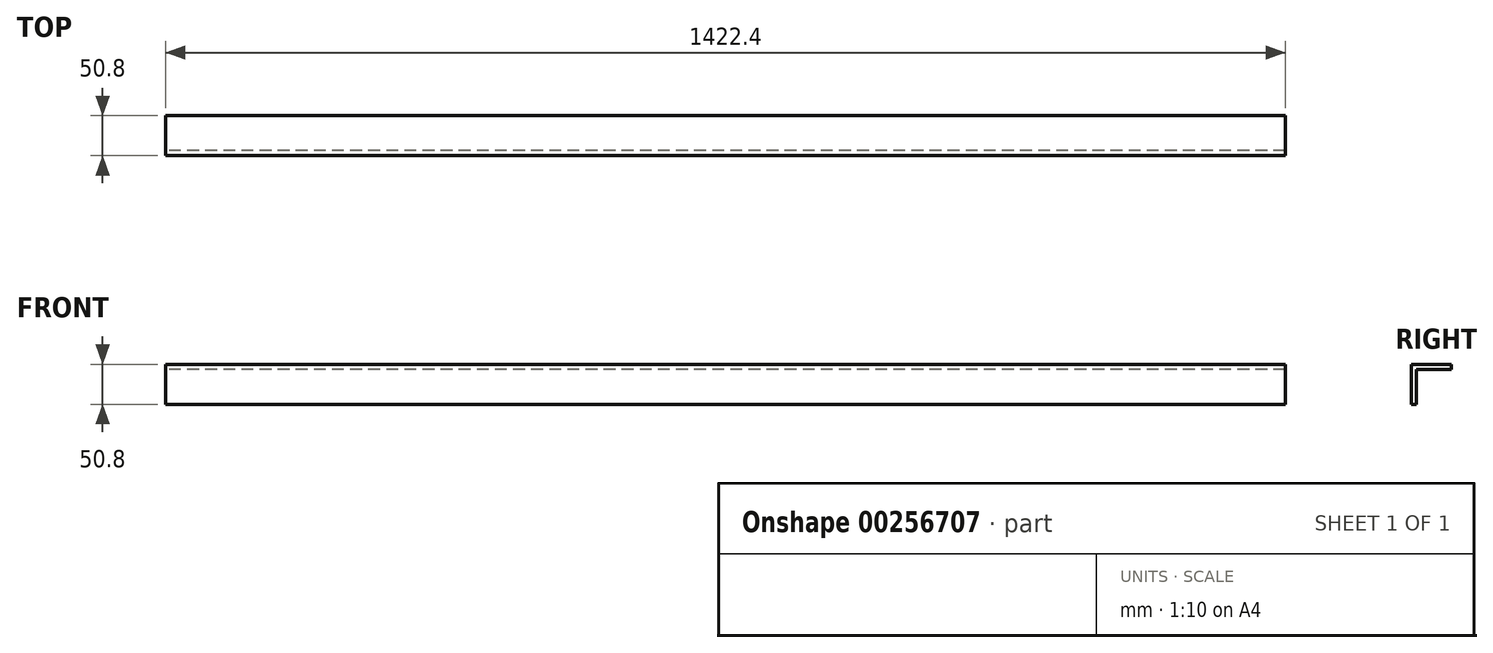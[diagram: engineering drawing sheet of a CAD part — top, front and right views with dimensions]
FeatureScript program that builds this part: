
annotation { "Feature Type Name" : "Feature", "Feature Type Description" : "" }
export const myFeature = defineFeature(function(context is Context, id is Id, definition is map)
    precondition{}
    {
        {
            var Q0;
            Q0=qCreatedBy(makeId("Right.planeOp"),FACE);
            var sketch = newSketch(context, id + "F0", { "sketchPlane" : qUnion([Q0])});
            skLineSegment(sketch, "E0", {"start": v(-30.37, -27.01) * mm, "end": v(-30.37, 23.79) * mm});
            skLineSegment(sketch, "E1", {"start": v(-30.37, 23.79) * mm, "end": v(20.43, 23.79) * mm});
            skLineSegment(sketch, "E2", {"start": v(20.43, 23.79) * mm, "end": v(20.43, 17.44) * mm});
            skLineSegment(sketch, "E3", {"start": v(20.43, 17.44) * mm, "end": v(-24.02, 17.44) * mm});
            skLineSegment(sketch, "E4", {"start": v(-30.37, -27.01) * mm, "end": v(-24.02, -27.01) * mm});
            skLineSegment(sketch, "E5", {"start": v(-24.02, -27.01) * mm, "end": v(-24.02, 17.44) * mm});
            skSolve(sketch);
        }
        {
            var Q0;
            Q0=makeQuery(id+"F0.imprint","IMPRINT",FACE,{"disambiguationData":[TD([[makeQuery(id+"F0.imprint","IMPRINT",EDGE,{"derivedFrom":sQuery(id+"F0.wireOp",EDGE,"E0")}),-1.0]])]});
            extrude(context, id + "F1", {"entities" : qUnion([Q0]), "depth" : 1422.4 * mm});
        }
    });
